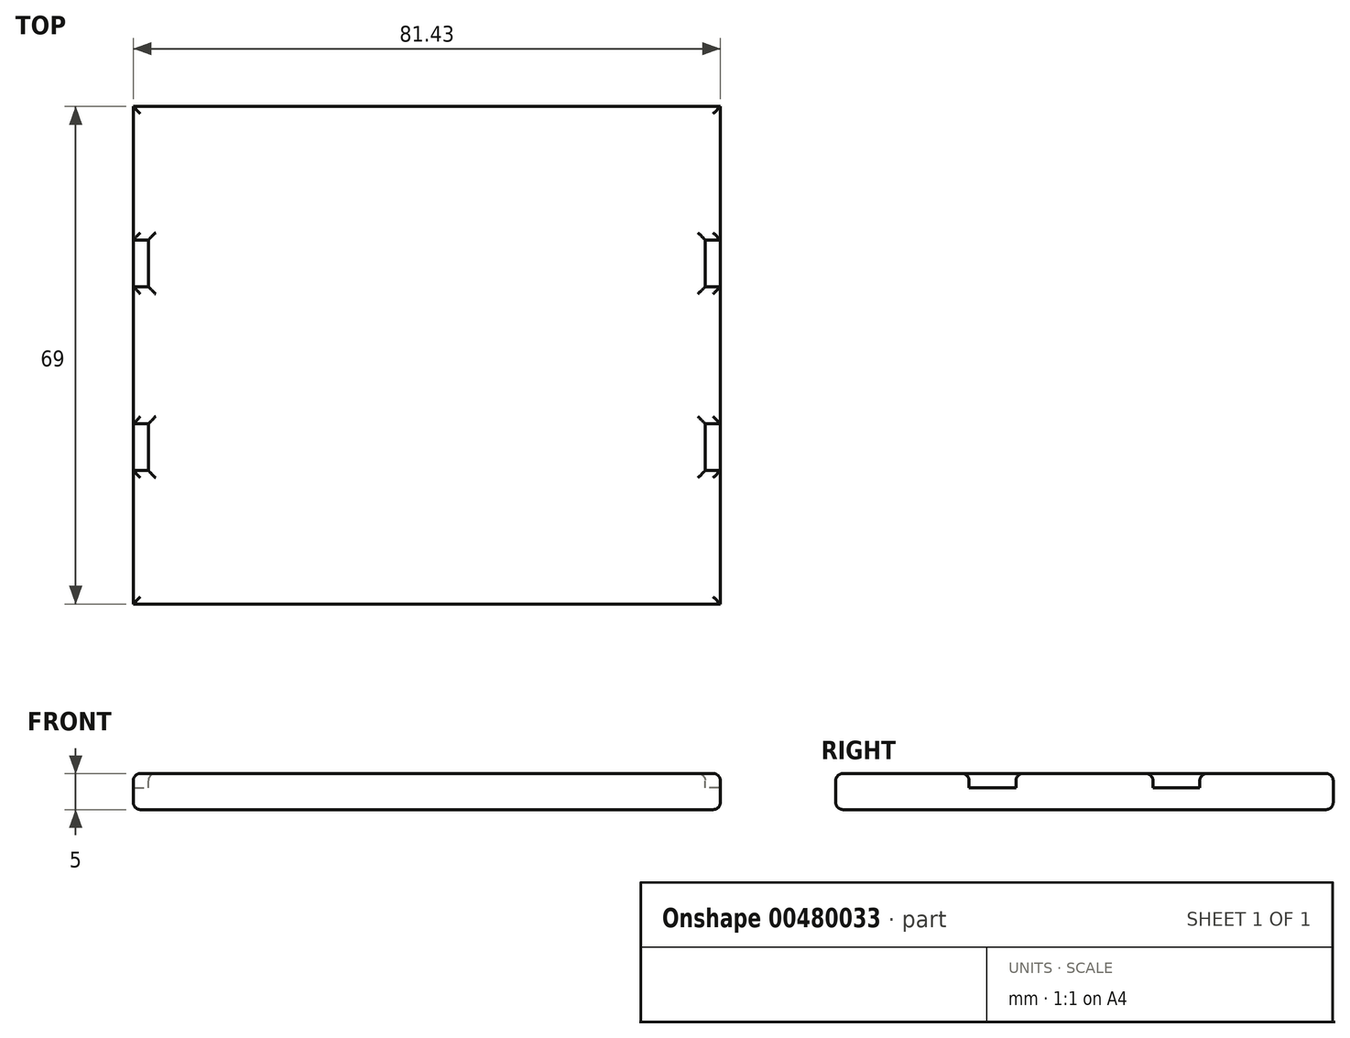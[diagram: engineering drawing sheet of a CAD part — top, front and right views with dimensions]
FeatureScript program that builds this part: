
annotation { "Feature Type Name" : "Feature", "Feature Type Description" : "" }
export const myFeature = defineFeature(function(context is Context, id is Id, definition is map)
    precondition{}
    {
        {
            var Q0;
            Q0=qCreatedBy(makeId("Top.planeOp"),FACE);
            var sketch = newSketch(context, id + "F0", { "sketchPlane" : qUnion([Q0])});
            skLineSegment(sketch, "E0.bottom", {"start": v(-35.73, 39.82) * mm, "end": v(45.7, 39.82) * mm});
            skLineSegment(sketch, "E0.top", {"start": v(-35.73, -29.18) * mm, "end": v(45.7, -29.18) * mm});
            skLineSegment(sketch, "E0.left", {"start": v(-35.73, 39.82) * mm, "end": v(-35.73, -29.18) * mm});
            skLineSegment(sketch, "E0.right", {"start": v(45.7, 39.82) * mm, "end": v(45.7, -29.18) * mm});
            skSolve(sketch);
        }
        {
            var Q0;
            Q0=qSketchRegion(id+"F0",true);
            extrude(context, id + "F1", {"entities" : qUnion([Q0]), "depth" : 5 * mm});
        }
        {
            var Q0;
            Q0=makeQuery(id+"F1.opExtrude","CAP_FACE",FACE,{"disambiguationData":[OSD([sQuery(id+"F0.wireOp",EDGE,"E0.bottom"),sQuery(id+"F0.wireOp",EDGE,"E0.top"),sQuery(id+"F0.wireOp",EDGE,"E0.left"),sQuery(id+"F0.wireOp",EDGE,"E0.right")])],"isStart":false});
            var sketch = newSketch(context, id + "F2", { "sketchPlane" : qUnion([Q0])});
            skPoint(sketch, "E1", {"position": v(-35.73, -10.68) * mm});
            skPoint(sketch, "E2", {"position": v(-35.73, 21.32) * mm});
            skPoint(sketch, "E3", {"position": v(-35.73, 5.32) * mm});
            skPoint(sketch, "E4", {"position": v(-35.73, 14.82) * mm});
            skPoint(sketch, "E5", {"position": v(-35.73, -4.18) * mm});
            skLineSegment(sketch, "E6.bottom", {"start": v(-35.73, 21.32) * mm, "end": v(-33.63, 21.32) * mm});
            skLineSegment(sketch, "E6.top", {"start": v(-35.73, 14.82) * mm, "end": v(-33.63, 14.82) * mm});
            skLineSegment(sketch, "E6.left", {"start": v(-35.73, 21.32) * mm, "end": v(-35.73, 14.82) * mm});
            skLineSegment(sketch, "E6.right", {"start": v(-33.63, 21.32) * mm, "end": v(-33.63, 14.82) * mm});
            skLineSegment(sketch, "E7.bottom", {"start": v(-35.73, -4.18) * mm, "end": v(-33.63, -4.18) * mm});
            skLineSegment(sketch, "E7.top", {"start": v(-35.73, -10.68) * mm, "end": v(-33.63, -10.68) * mm});
            skLineSegment(sketch, "E7.left", {"start": v(-35.73, -4.18) * mm, "end": v(-35.73, -10.68) * mm});
            skLineSegment(sketch, "E7.right", {"start": v(-33.63, -4.18) * mm, "end": v(-33.63, -10.68) * mm});
            skLineSegment(sketch, "E8", {"start": v(-35.73, 21.32) * mm, "end": v(45.7, 21.32) * mm, "construction": true});
            skLineSegment(sketch, "E9", {"start": v(-35.73, 14.82) * mm, "end": v(45.7, 14.82) * mm, "construction": true});
            skLineSegment(sketch, "E10", {"start": v(-35.73, -4.18) * mm, "end": v(45.7, -4.18) * mm, "construction": true});
            skLineSegment(sketch, "E11", {"start": v(-35.73, -10.68) * mm, "end": v(45.7, -10.68) * mm, "construction": true});
            skLineSegment(sketch, "E12.bottom", {"start": v(45.7, 21.32) * mm, "end": v(43.6, 21.32) * mm});
            skLineSegment(sketch, "E12.top", {"start": v(45.7, 14.82) * mm, "end": v(43.6, 14.82) * mm});
            skLineSegment(sketch, "E12.left", {"start": v(45.7, 21.32) * mm, "end": v(45.7, 14.82) * mm});
            skLineSegment(sketch, "E12.right", {"start": v(43.6, 21.32) * mm, "end": v(43.6, 14.82) * mm});
            skLineSegment(sketch, "E13.bottom", {"start": v(45.7, -4.18) * mm, "end": v(43.6, -4.18) * mm});
            skLineSegment(sketch, "E13.top", {"start": v(45.7, -10.68) * mm, "end": v(43.6, -10.68) * mm});
            skLineSegment(sketch, "E13.left", {"start": v(45.7, -4.18) * mm, "end": v(45.7, -10.68) * mm});
            skLineSegment(sketch, "E13.right", {"start": v(43.6, -4.18) * mm, "end": v(43.6, -10.68) * mm});
            skSolve(sketch);
        }
        {
            var Q0;
            Q0=qSketchRegion(id+"F2",true);
            extrude(context, id + "F3", {"entities" : qUnion([Q0]), "operationType" : NewBodyOperationType.REMOVE, "oppositeDirection" : true, "depth" : 2 * mm});
        }
        {
            var Q0;
            Q0=makeQuery(id+"F1.opExtrude","CAP_FACE",FACE,{"disambiguationData":[OSD([sQuery(id+"F0.wireOp",EDGE,"E0.bottom"),sQuery(id+"F0.wireOp",EDGE,"E0.top"),sQuery(id+"F0.wireOp",EDGE,"E0.left"),sQuery(id+"F0.wireOp",EDGE,"E0.right")])],"isStart":false});
            var Q1;
            Q1=makeQuery(id+"F1.opExtrude","CAP_FACE",FACE,{"disambiguationData":[OSD([sQuery(id+"F0.wireOp",EDGE,"E0.bottom"),sQuery(id+"F0.wireOp",EDGE,"E0.top"),sQuery(id+"F0.wireOp",EDGE,"E0.left"),sQuery(id+"F0.wireOp",EDGE,"E0.right")])],"isStart":true});
            var Q2;
            Q2=makeQuery(id+"F3.opExtrude","SWEPT_FACE",FACE,{"disambiguationData":[OSD([sQuery(id+"F2.wireOp",EDGE,"E7.right")])]});
            var Q3;
            Q3=makeQuery(id+"F3.opExtrude","SWEPT_FACE",FACE,{"disambiguationData":[OSD([sQuery(id+"F2.wireOp",EDGE,"E6.right")])]});
            var Q4;
            Q4=makeQuery(id+"F3.opExtrude","SWEPT_FACE",FACE,{"disambiguationData":[OSD([sQuery(id+"F2.wireOp",EDGE,"E12.right")])]});
            var Q5;
            Q5=makeQuery(id+"F3.opExtrude","SWEPT_FACE",FACE,{"disambiguationData":[OSD([sQuery(id+"F2.wireOp",EDGE,"E13.right")])]});
            fillet(context, id + "F4", {"entities" : qUnion([Q0, Q1, Q2, Q3, Q4, Q5]), "radius" : 1 * mm, "tangentPropagation" : true, "allowEdgeOverflow" : false});
        }
    });
